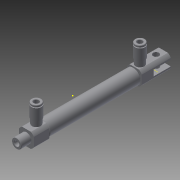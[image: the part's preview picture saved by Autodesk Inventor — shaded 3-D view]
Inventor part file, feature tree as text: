
AUTODESK INVENTOR PART (.ipt)
format: ipt  version: 2015 SP1 (Build 190203100, 203)  size: 324,096 bytes
history: native  units: in
note: dims shown in document units (in); Inventor stores cm internally (conversion verified against a paired STEP export)
features: other x5, imported_body x3, sketch x1
ambient origin geometry x8: Origin, YZ Plane, XZ Plane, XY Plane, X Axis, Y Axis, Z Axis, Center Point
bodies: Body1 (feature_tree), Body2 (feature_tree), Body3 (feature_tree)
feature tree (9):
  other  "Pneumatic Cylinder1"
  sketch  "Sketch1"  dims[d0=0.0in d1=0.0in d2=0.0in d3=0.0in d4=0.0in]
  other  "Work Axis1"
  other  "NONE_2"
  other  "Port"
  other  "Port_1"
  imported_body  "Base3"
  imported_body  "Base4"
  imported_body  "Base5"
